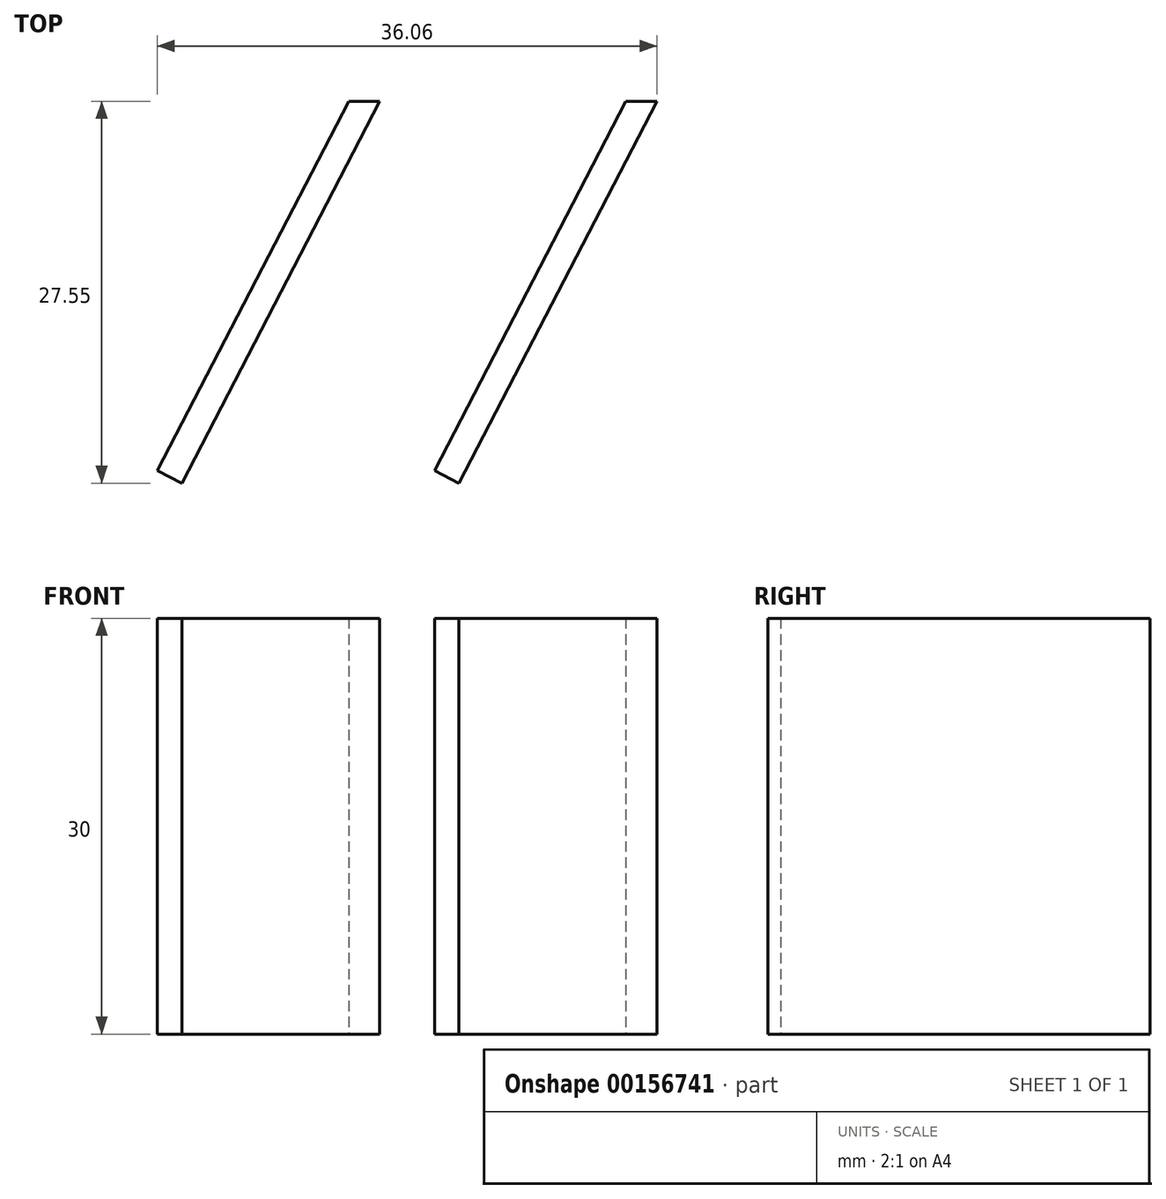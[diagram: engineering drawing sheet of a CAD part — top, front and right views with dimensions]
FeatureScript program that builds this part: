
annotation { "Feature Type Name" : "Feature", "Feature Type Description" : "" }
export const myFeature = defineFeature(function(context is Context, id is Id, definition is map)
    precondition{}
    {
        {
            var Q0;
            Q0=qCreatedBy(makeId("Front.planeOp"),FACE);
            var sketch = newSketch(context, id + "F0", { "sketchPlane" : qUnion([Q0])});
            skLineSegment(sketch, "E0.bottom", {"start": v(0, 0) * mm, "end": v(-40, 0) * mm});
            skLineSegment(sketch, "E0.top", {"start": v(0, 40) * mm, "end": v(-40, 40) * mm});
            skLineSegment(sketch, "E0.left", {"start": v(0, 0) * mm, "end": v(0, 40) * mm});
            skLineSegment(sketch, "E0.right", {"start": v(-40, 0) * mm, "end": v(-40, 40) * mm});
            skSolve(sketch);
        }
        {
            var Q0;
            Q0=qCreatedBy(makeId("Top.planeOp"),FACE);
            var sketch = newSketch(context, id + "F1", { "sketchPlane" : qUnion([Q0])});
            skLineSegment(sketch, "E1", {"start": v(-37.83, 0) * mm, "end": v(-51.64, -26.63) * mm});
            skLineSegment(sketch, "E2", {"start": v(-51.64, -26.63) * mm, "end": v(-49.86, -27.55) * mm});
            skLineSegment(sketch, "E3", {"start": v(-49.86, -27.55) * mm, "end": v(-35.58, 0) * mm});
            skLineSegment(sketch, "E4", {"start": v(-25.58, 0) * mm, "end": v(-48.25, -43.73) * mm, "construction": true});
            skLineSegment(sketch, "E5.1.0.0", {"start": v(-17.83, 0) * mm, "end": v(-31.64, -26.63) * mm});
            skLineSegment(sketch, "E5.1.0.1", {"start": v(-29.86, -27.55) * mm, "end": v(-15.58, 0) * mm});
            skLineSegment(sketch, "E5.1.0.2", {"start": v(-31.64, -26.63) * mm, "end": v(-29.86, -27.55) * mm});
            skLineSegment(sketch, "E5.direction1", {"start": v(-51.64, -26.63) * mm, "end": v(-31.64, -26.63) * mm, "construction": true});
            skLineSegment(sketch, "E6", {"start": v(-37.83, 0) * mm, "end": v(-35.58, 0) * mm});
            skLineSegment(sketch, "E7", {"start": v(-17.83, 0) * mm, "end": v(-15.58, 0) * mm});
            skSolve(sketch);
        }
        {
            var Q0;
            Q0=makeQuery(id+"F1.imprint","IMPRINT",FACE,{"disambiguationData":[TD([[makeQuery(id+"F1.imprint","IMPRINT",EDGE,{"derivedFrom":sQuery(id+"F1.wireOp",EDGE,"E1")}),1.0]])]});
            extrude(context, id + "F2", {"entities" : qUnion([Q0]), "depth" : 30 * mm});
        }
        {
            var Q0;
            Q0=makeQuery(id+"F1.imprint","IMPRINT",FACE,{"disambiguationData":[TD([[makeQuery(id+"F1.imprint","IMPRINT",EDGE,{"derivedFrom":sQuery(id+"F1.wireOp",EDGE,"E5.1.0.0")}),1.0]])]});
            extrude(context, id + "F3", {"entities" : qUnion([Q0]), "depth" : 30 * mm});
        }
    });
